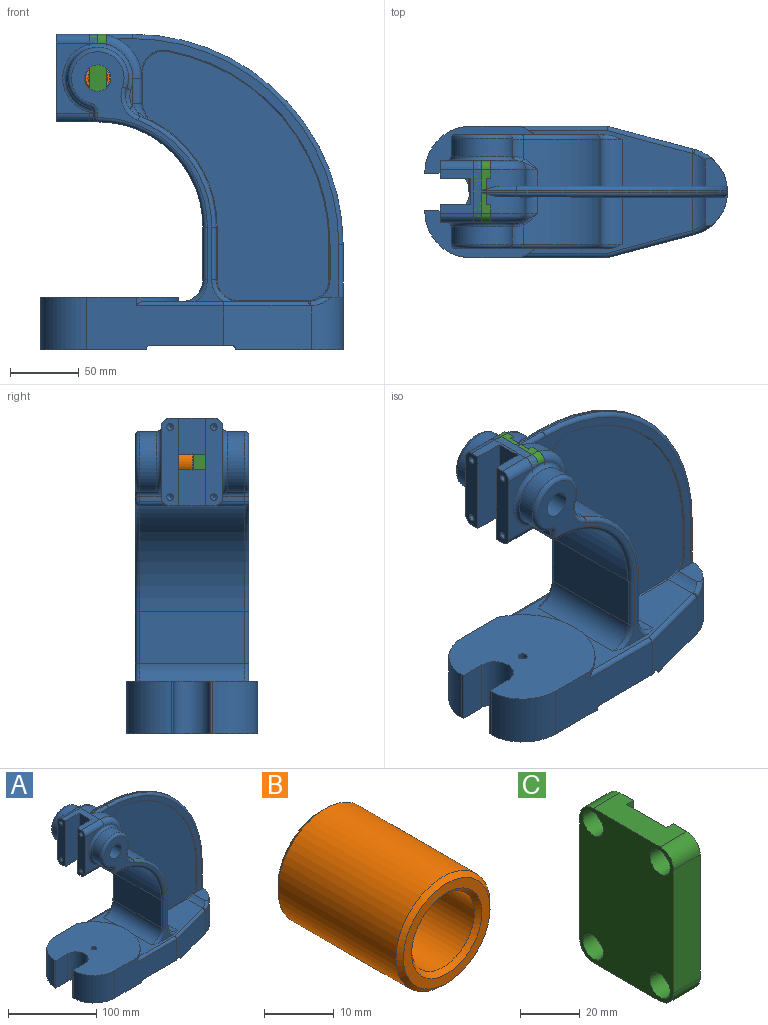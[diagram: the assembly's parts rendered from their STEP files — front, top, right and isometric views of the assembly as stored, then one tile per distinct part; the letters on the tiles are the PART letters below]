
ASSEMBLY  parts=3 mates=2
PART A: 180 faces, bbox 234.5x98.1x244 mm
  f0: plane 63.5x12.7mm, normal (-1,0,0), area 753.5mm2, adj f2,f15,f17,f92,f97,f149,f151,f158
  f1: plane 20.23x2.34mm, normal (0,1,0), area 23.9mm2, adj f90,f91,f104,f106
  f2: plane 50.8x30.1mm, normal (0,-1,0), area 515.4mm2, adj f0,f83,f92,f97,f124
  f3: plane 22.59x12.73mm, normal (1,0,0), area 235.4mm2, adj f19,f26,f32,f87,f94,f174
  f4: plane 22.59x12.73mm, normal (1,0,0), area 235.4mm2, adj f10,f14,f33,f86,f90,f164
  f5: plane 99.19x38.1mm, normal (0,-1,0), area 3202mm2, adj f6,f40,f46,f49,f52,f58,f76,f133
  f6: plane 100x95.25mm, normal (0,0,1), area 7398mm2, adj f5,f43,f44,f48,f54,f55,f56,f57
  f7: plane 38.1x34.96mm, normal (1,0,0), area 1331.9mm2, adj f8,f9,f114,f169
  f8: cylinder r=15.88mm len=34.96mm, axis (0,1,0), area 871.7mm2, adj f7,f37,f115,f167
  f9: cylinder r=85.72mm len=80.21mm, axis (0,1,0), area 3442.3mm2, adj f7,f80,f86,f100,f113,f168
  f10: cylinder r=15.88mm len=18.65mm, axis (0,1,0), area 22.7mm2, adj f4,f11,f33,f162
  f11: cylinder r=142.88mm len=140.67mm, axis (0,1,0), area 163.3mm2, adj f10,f12,f33,f160
  f12: plane 25.4x0.82mm, normal (-1,0,0), area 20.8mm2, adj f11,f13,f33,f161
  f13: cylinder r=15.88mm len=24.81mm, axis (0,1,0), area 242.1mm2, adj f12,f33,f37,f45,f139,f140,f163
  f14: cylinder r=31.75mm len=31.75mm, axis (0,1,0), area 616.8mm2, adj f4,f15,f33,f89,f141
  f15: plane 55.5x31.75mm, normal (0,0,1), area 573.2mm2, adj f0,f14,f16,f19,f31,f88,f92,f141
  f16: plane 63.5x12.7mm, normal (-1,0,0), area 753.5mm2, adj f15,f17,f21,f88,f96,f147,f153,f157
  f17: plane 31.75x30.1mm, normal (0,0,-1), area 533.2mm2, adj f0,f16,f18,f96,f97,f156,f157,f158
  f18: cylinder r=76.2mm len=76.2mm, axis (0,1,0), area 9120.7mm2, adj f17,f22,f103,f105,f119,f121
  f19: cylinder r=31.75mm len=31.75mm, axis (0,1,0), area 616.8mm2, adj f3,f15,f32,f93,f144
  f20: plane 20.23x2.34mm, normal (0,-1,0), area 23.9mm2, adj f94,f95,f122,f124
  f21: plane 50.8x30.1mm, normal (0,1,0), area 515.4mm2, adj f16,f78,f88,f96,f106
  f22: plane 76.2x38.1mm, normal (-1,0,0), area 2903.2mm2, adj f18,f98,f101,f117
  f23: cylinder r=15.88mm len=34.96mm, axis (0,1,0), area 871.7mm2, adj f24,f37,f132,f177
  f24: plane 38.1x34.96mm, normal (1,0,0), area 1331.9mm2, adj f23,f25,f131,f179
  f25: cylinder r=85.72mm len=80.21mm, axis (0,1,0), area 3442.3mm2, adj f24,f81,f87,f118,f130,f178
  f26: cylinder r=15.88mm len=18.65mm, axis (0,1,0), area 22.7mm2, adj f3,f27,f32,f172
  f27: cylinder r=142.88mm len=140.67mm, axis (0,1,0), area 163.3mm2, adj f26,f28,f32,f170
  f28: plane 25.4x0.82mm, normal (-1,0,0), area 20.8mm2, adj f27,f29,f32,f171
  f29: cylinder r=15.88mm len=24.81mm, axis (0,1,0), area 242.1mm2, adj f28,f32,f36,f37,f135,f136,f173
  f30: plane 76.2x7.92mm, normal (1,0,0), area 361.9mm2, adj f31,f36,f42,f45,f51,f53,f143,f146
  f31: cylinder r=152.4mm len=152.4mm, axis (0,1,0), area 377mm2, adj f15,f30,f142,f145
  f32: plane 187.33x160.79mm, normal (0,-1,0), area 1900.4mm2, adj f3,f19,f26,f27,f28,f29,f36,f144
  f33: plane 187.33x160.79mm, normal (0,1,0), area 1900.4mm2, adj f4,f10,f11,f12,f13,f14,f45,f141
  f34: plane 180.67x135mm, normal (0,-1,0), area 14138.8mm2, adj f170,f171,f172,f173,f174,f175,f176,f177
  f35: plane 180.67x135mm, normal (0,1,0), area 14138.8mm2, adj f160,f161,f162,f163,f164,f165,f166,f167
  f36: plane 26.58x18.73mm, normal (0,0,1), area 245.8mm2, adj f29,f30,f32,f53,f136,f146
  f37: plane 119.12x89.67mm, normal (0,0,1), area 4280.2mm2, adj f8,f13,f23,f29,f76,f77,f84,f98
  f38: cylinder r=3.17mm len=9.06mm, axis (0,1,0), area 40.9mm2, adj f40,f42,f52,f69
  f39: cylinder r=3.17mm len=7.93mm, axis (0,1,0), area 39.5mm2, adj f41,f46,f48,f65
  f40: plane 58.73x9.7mm, normal (0,0,-1), area 467.1mm2, adj f5,f38,f49,f52,f64,f69
  f41: plane 58.73x9.7mm, normal (0,0,-1), area 467.1mm2, adj f39,f47,f48,f50,f65,f67
  f42: plane 90.55x77.8mm, normal (0,0,-1), area 1454mm2, adj f30,f38,f47,f50,f51,f52,f53,f59
  f43: plane 38.1x1.61mm, normal (-1,0,0), area 61.5mm2, adj f6,f46,f54,f58
  f44: plane 38.1x1.61mm, normal (-1,0,0), area 61.5mm2, adj f6,f46,f55,f57
  f45: plane 26.58x18.73mm, normal (0,0,1), area 245.8mm2, adj f13,f30,f33,f51,f140,f143
  f46: plane 95.25x76.2mm, normal (0,0,-1), area 2029.8mm2, adj f5,f39,f43,f44,f48,f49,f54,f55
  f47: cylinder r=3.17mm len=9.06mm, axis (0,1,0), area 40.9mm2, adj f41,f42,f50,f67
  f48: plane 99.19x38.1mm, normal (0,1,0), area 3202mm2, adj f6,f39,f41,f46,f50,f57,f76,f137
  f49: cylinder r=3.17mm len=7.93mm, axis (0,1,0), area 39.5mm2, adj f5,f40,f46,f64
  f50: plane 63.64x32.15mm, normal (0.26,0.97,0), area 2053.6mm2, adj f41,f42,f47,f48,f51,f138,f139
  f51: cylinder r=31.75mm len=38.1mm, axis (0,0,-1), area 1379.2mm2, adj f30,f42,f45,f50,f140
  f52: plane 63.64x32.15mm, normal (0.26,-0.97,0), area 2053.6mm2, adj f5,f38,f40,f42,f53,f134,f135
  f53: cylinder r=31.75mm len=38.1mm, axis (0,0,-1), area 1379.2mm2, adj f30,f36,f42,f52,f136
  f54: plane 38.1x19.05mm, normal (0,1,0), area 725.8mm2, adj f6,f43,f46,f56
  f55: plane 38.1x19.05mm, normal (0,-1,0), area 725.8mm2, adj f6,f44,f46,f56
  f56: cylinder r=13.49mm len=38.1mm, axis (0,0,-1), area 1615.1mm2, adj f6,f46,f54,f55
  f57: cylinder r=33.32mm len=38.1mm, axis (0,0,-1), area 1963.7mm2, adj f6,f44,f46,f48
  f58: cylinder r=33.32mm len=38.1mm, axis (0,0,-1), area 1963.7mm2, adj f5,f6,f43,f46
  f59: plane 30.18x6.86mm, normal (-1,0,0), area 207mm2, adj f42,f60,f68,f70
  f60: plane 31.27x5.6mm, normal (0,0,-1), area 124.1mm2, adj f59,f61,f68,f70
  f61: cylinder r=23.8mm len=46.06mm, axis (0,1,0), area 499.2mm2, adj f60,f62,f67,f68,f69,f70
  f62: plane 84.13x79.4mm, normal (0,0,-1), area 5642.5mm2, adj f61,f64,f65,f66,f67,f69
  f63: plane 100.62x79.4mm, normal (0,0,-1), area 6568.5mm2, adj f64,f65,f66,f71,f72,f73,f74,f75
  f64: plane 98.15x30.18mm, normal (0,1,0), area 2718.8mm2, adj f40,f46,f49,f62,f63,f66,f69,f75
  f65: plane 98.15x30.18mm, normal (0,-1,0), area 2718.8mm2, adj f39,f41,f46,f62,f63,f66,f67,f74
  f66: plane 79.4x3.18mm, normal (-1,0,0), area 252.1mm2, adj f62,f63,f64,f65
  f67: plane 62.63x27.36mm, normal (-0.26,-0.97,0), area 1710.8mm2, adj f41,f42,f47,f61,f62,f65,f68
  f68: cylinder r=23.83mm len=30.18mm, axis (0,0,-1), area 814.8mm2, adj f42,f59,f60,f61,f67
  f69: plane 62.63x27.36mm, normal (-0.26,0.97,0), area 1710.8mm2, adj f38,f40,f42,f61,f62,f64,f70
  f70: cylinder r=23.83mm len=30.18mm, axis (0,0,-1), area 814.8mm2, adj f42,f59,f60,f61,f69
  f71: plane 30.18x10.12mm, normal (0,-1,0), area 305.3mm2, adj f46,f63,f73,f75
  f72: plane 30.18x10.12mm, normal (0,1,0), area 305.3mm2, adj f46,f63,f73,f74
  f73: cylinder r=21.42mm len=42.84mm, axis (0,0,-1), area 2030.4mm2, adj f46,f63,f71,f72
  f74: cylinder r=25.4mm len=30.18mm, axis (0,0,-1), area 986.2mm2, adj f46,f63,f65,f72
  f75: cylinder r=25.4mm len=30.18mm, axis (0,0,-1), area 986.2mm2, adj f46,f63,f64,f71
  f76: cylinder r=52.37mm len=95.25mm, axis (0,0,1), area 401mm2, adj f5,f6,f37,f48,f133,f137
  f77: plane 180.98x110.12mm, normal (0,1,0), area 1717.8mm2, adj f37,f85,f99,f101,f103,f109,f110,f111
  f78: plane 16.73x3.98mm, normal (-1,0,0), area 64.1mm2, adj f21,f96,f105,f106,f108,f109
  f79: cylinder r=22.23mm len=44.45mm, axis (0,1,0), area 1356.2mm2, adj f80,f106,f108,f111
  f80: cylinder r=15.88mm len=20.22mm, axis (0,1,0), area 319.4mm2, adj f9,f79,f102,f104,f112
  f81: cylinder r=15.88mm len=20.22mm, axis (0,1,0), area 319.4mm2, adj f25,f82,f120,f122,f129
  f82: cylinder r=22.23mm len=44.45mm, axis (0,1,0), area 1356.2mm2, adj f81,f124,f126,f128
  f83: plane 16.73x3.98mm, normal (-1,0,0), area 64.1mm2, adj f2,f97,f121,f124,f125,f126
  f84: plane 180.98x110.12mm, normal (0,-1,0), area 1717.8mm2, adj f37,f85,f116,f117,f119,f125,f127,f128
  f85: cylinder r=9.53mm len=82.55mm, axis (0,1,0), area 4727mm2, adj f77,f84,f156,f157,f158,f159
  f86: cylinder r=15.88mm len=14.02mm, axis (0,1,0), area 218.9mm2, adj f4,f9,f91,f166
  f87: cylinder r=15.88mm len=14.02mm, axis (0,1,0), area 218.9mm2, adj f3,f25,f95,f176
  f88: cylinder r=6.35mm len=30.1mm, axis (-1,0,0), area 300.2mm2, adj f15,f16,f21,f89
  f89: torus R=25.4mm, axis (0,-1,0), area 461.3mm2, adj f14,f88,f90,f106
  f90: cylinder r=6.35mm len=18.2mm, axis (0,0,1), area 181.6mm2, adj f1,f4,f89,f91
  f91: torus R=22.23mm, axis (0,-1,0), area 98mm2, adj f1,f86,f90,f100,f102
  f92: cylinder r=6.35mm len=30.1mm, axis (1,0,0), area 300.2mm2, adj f0,f2,f15,f93
  f93: torus R=25.4mm, axis (0,-1,0), area 461.3mm2, adj f19,f92,f94,f124
  f94: cylinder r=6.35mm len=18.2mm, axis (0,0,-1), area 181.6mm2, adj f3,f20,f93,f95
  f95: torus R=22.23mm, axis (0,-1,0), area 98mm2, adj f20,f87,f94,f118,f120
  f96: cylinder r=6.35mm len=30.1mm, axis (1,0,0), area 279.1mm2, adj f16,f17,f21,f78,f105
  f97: cylinder r=6.35mm len=30.1mm, axis (-1,0,0), area 279.1mm2, adj f0,f2,f17,f83,f121
  f98: cylinder r=15.88mm len=76.2mm, axis (0,-1,0), area 1900.2mm2, adj f22,f37,f99,f116
  f99: torus R=19.05mm, axis (0,-1,0), area 107.7mm2, adj f37,f77,f98,f101
  f100: bspline ~12.01x8.85mm, area 17.9mm2, adj f9,f91,f102
  f101: cylinder r=3.17mm len=38.1mm, axis (0,0,-1), area 190mm2, adj f22,f77,f99,f103
  f102: bspline ~10.6x9.56mm, area 36.6mm2, adj f80,f91,f100,f104
  f103: torus R=79.38mm, axis (0,-1,0), area 606mm2, adj f18,f77,f101,f107
  f104: torus R=12.7mm, axis (0,-1,0), area 70.6mm2, adj f1,f80,f102,f106
  f105: cylinder r=3.17mm len=22.23mm, axis (0,1,0), area 97.1mm2, adj f18,f78,f96,f107
  f106: torus R=25.4mm, axis (0,-1,0), area 570mm2, adj f1,f21,f78,f79,f89,f104,f108
  f107: sphere r=3.17mm, area 21.6mm2, adj f103,f105,f109
  f108: cylinder r=3.17mm len=15.82mm, axis (0,1,0), area 59.7mm2, adj f78,f79,f106,f110
  f109: cylinder r=3.17mm len=3.98mm, axis (0,0,-1), area 19.9mm2, adj f77,f78,f107,f110
  f110: torus R=6.35mm, axis (0,-1,0), area 28.5mm2, adj f77,f108,f109,f111
  f111: torus R=19.05mm, axis (0,-1,0), area 504.9mm2, adj f77,f79,f110,f112
  f112: torus R=19.05mm, axis (0,-1,0), area 132.1mm2, adj f77,f80,f111,f113
  f113: torus R=82.55mm, axis (0,-1,0), area 510.4mm2, adj f9,f77,f112,f114
  f114: cylinder r=3.17mm len=38.1mm, axis (0,0,1), area 190mm2, adj f7,f77,f113,f115
  f115: torus R=19.05mm, axis (0,-1,0), area 107.7mm2, adj f8,f37,f77,f114
  f116: torus R=19.05mm, axis (0,-1,0), area 107.7mm2, adj f37,f84,f98,f117
  f117: cylinder r=3.17mm len=38.1mm, axis (0,0,1), area 190mm2, adj f22,f84,f116,f119
  f118: bspline ~11.06x8.44mm, area 17.9mm2, adj f25,f95,f120
  f119: torus R=79.38mm, axis (0,-1,0), area 606mm2, adj f18,f84,f117,f123
  f120: bspline ~9.12x8.99mm, area 36.6mm2, adj f81,f95,f118,f122
  f121: cylinder r=3.17mm len=22.23mm, axis (0,1,0), area 97.1mm2, adj f18,f83,f97,f123
  f122: torus R=12.7mm, axis (0,-1,0), area 70.6mm2, adj f20,f81,f120,f124
  f123: sphere r=3.17mm, area 15.8mm2, adj f119,f121,f125
  f124: torus R=25.4mm, axis (0,-1,0), area 570mm2, adj f2,f20,f82,f83,f93,f122,f126
  f125: cylinder r=3.17mm len=3.98mm, axis (0,0,1), area 19.9mm2, adj f83,f84,f123,f127
  f126: cylinder r=3.17mm len=15.82mm, axis (0,1,0), area 59.7mm2, adj f82,f83,f124,f127
  f127: torus R=6.35mm, axis (0,-1,0), area 28.5mm2, adj f84,f125,f126,f128
  f128: torus R=19.05mm, axis (0,-1,0), area 504.9mm2, adj f82,f84,f127,f129
  f129: torus R=19.05mm, axis (0,-1,0), area 132.1mm2, adj f81,f84,f128,f130
  f130: torus R=82.55mm, axis (0,-1,0), area 510.4mm2, adj f25,f84,f129,f131
  f131: cylinder r=3.17mm len=38.1mm, axis (0,0,-1), area 190mm2, adj f24,f84,f130,f132
  f132: torus R=19.05mm, axis (0,-1,0), area 107.7mm2, adj f23,f37,f84,f131
  f133: cylinder r=3.17mm len=63.09mm, axis (1,0,0), area 298.9mm2, adj f5,f37,f76,f134
  f134: cylinder r=3.17mm len=62.81mm, axis (0.97,0.26,0), area 319mm2, adj f37,f52,f133,f135
  f135: bspline ~3.41x3.21mm, area 6mm2, adj f29,f52,f134,f136
  f136: bspline ~18.95x11.92mm, area 79.7mm2, adj f29,f36,f53,f135
  f137: cylinder r=3.17mm len=63.09mm, axis (-1,0,0), area 298.9mm2, adj f37,f48,f76,f138
  f138: cylinder r=3.17mm len=62.81mm, axis (-0.97,0.26,0), area 319mm2, adj f37,f50,f137,f139
  f139: bspline ~6.89x4.84mm, area 6mm2, adj f13,f50,f138,f140
  f140: bspline ~17.46x11.57mm, area 79.7mm2, adj f13,f45,f51,f139
  f141: cylinder r=3.17mm len=25.4mm, axis (-1,0,0), area 92.2mm2, adj f14,f15,f33,f142
  f142: torus R=149.22mm, axis (0,-1,0), area 1184.9mm2, adj f31,f33,f141,f143
  f143: cylinder r=3.17mm len=38.1mm, axis (0,0,1), area 190mm2, adj f30,f33,f45,f142
  f144: cylinder r=3.17mm len=25.4mm, axis (1,0,0), area 92.2mm2, adj f15,f19,f32,f145
  f145: torus R=149.22mm, axis (0,-1,0), area 1184.9mm2, adj f31,f32,f144,f146
  f146: cylinder r=3.17mm len=38.1mm, axis (0,0,-1), area 190mm2, adj f30,f32,f36,f145
  f147: cylinder r=2.38mm len=6.35mm, axis (-1,0,0), area 95mm2, adj f16,f148
  f148: cone r=0mm half-angle=59deg, axis (-1,0,0), area 20.8mm2, adj f147
  f149: cylinder r=2.38mm len=6.35mm, axis (-1,0,0), area 95mm2, adj f0,f150
  f150: cone r=0mm half-angle=59deg, axis (-1,0,0), area 20.8mm2, adj f149
  f151: cylinder r=2.38mm len=6.35mm, axis (-1,0,0), area 95mm2, adj f0,f152
  f152: cone r=0mm half-angle=59deg, axis (-1,0,0), area 20.8mm2, adj f151
  f153: cylinder r=2.38mm len=6.35mm, axis (-1,0,0), area 95mm2, adj f16,f154
  f154: cone r=0mm half-angle=59deg, axis (-1,0,0), area 20.8mm2, adj f153
  f155: cylinder r=3.17mm len=7.93mm, axis (0,0,1), area 158.1mm2, adj f6,f63
  f156: plane 26.47x19.05mm, normal (-1,0,0), area 504.2mm2, adj f17,f85,f157,f158
  f157: plane 63.5x22.17mm, normal (0,-1,0), area 1396.6mm2, adj f15,f16,f17,f85,f156,f159
  f158: plane 63.5x22.17mm, normal (0,1,0), area 1396.6mm2, adj f0,f15,f17,f85,f156,f159
  f159: plane 26.47x19.05mm, normal (-1,0,0), area 504.2mm2, adj f15,f85,f157,f158
  f160: torus R=142.11mm, axis (0,-1,0), area 238.1mm2, adj f11,f35,f161,f162
  f161: cylinder r=0.76mm len=25.4mm, axis (0,0,1), area 30.4mm2, adj f12,f35,f160,f163
  f162: torus R=15.11mm, axis (0,-1,0), area 32.6mm2, adj f10,f35,f160,f164
  f163: torus R=15.11mm, axis (0,-1,0), area 29.3mm2, adj f13,f35,f161,f165
  f164: cylinder r=0.76mm len=22.59mm, axis (0,0,1), area 27mm2, adj f4,f35,f162,f166
  f165: cylinder r=0.76mm len=50.8mm, axis (1,0,0), area 60.8mm2, adj f35,f37,f163,f167
  f166: torus R=15.11mm, axis (0,-1,0), area 20.2mm2, adj f35,f86,f164,f168
  f167: torus R=15.11mm, axis (0,-1,0), area 29.3mm2, adj f8,f35,f165,f169
  f168: torus R=86.49mm, axis (0,-1,0), area 111.5mm2, adj f9,f35,f166,f169
  f169: cylinder r=0.76mm len=38.1mm, axis (0,0,-1), area 45.6mm2, adj f7,f35,f167,f168
  f170: torus R=142.11mm, axis (0,-1,0), area 238.1mm2, adj f27,f34,f171,f172
  f171: cylinder r=0.76mm len=25.4mm, axis (0,0,-1), area 30.4mm2, adj f28,f34,f170,f173
  f172: torus R=15.11mm, axis (0,-1,0), area 32.6mm2, adj f26,f34,f170,f174
  f173: torus R=15.11mm, axis (0,-1,0), area 29.3mm2, adj f29,f34,f171,f175
  f174: cylinder r=0.76mm len=22.59mm, axis (0,0,-1), area 27mm2, adj f3,f34,f172,f176
  f175: cylinder r=0.76mm len=50.8mm, axis (-1,0,0), area 60.8mm2, adj f34,f37,f173,f177
  f176: torus R=15.11mm, axis (0,-1,0), area 20.2mm2, adj f34,f87,f174,f178
  f177: torus R=15.11mm, axis (0,-1,0), area 29.3mm2, adj f23,f34,f175,f179
  f178: torus R=86.49mm, axis (0,-1,0), area 111.5mm2, adj f25,f34,f176,f179
  f179: cylinder r=0.76mm len=38.1mm, axis (0,0,1), area 45.6mm2, adj f24,f34,f177,f178
PART B: 8 faces, bbox 19.1x25.4x19.1 mm
  f0: plane 17.53x17.53mm, normal (0,-1,0), area 82.3mm2, adj f4,f5
  f1: plane 17.53x17.53mm, normal (0,1,0), area 82.3mm2, adj f6,f7
  f2: cylinder r=9.53mm len=23.88mm, axis (0,1,0), area 1428.9mm2, adj f4,f7
  f3: cylinder r=6.35mm len=23.88mm, axis (0,1,0), area 952.6mm2, adj f5,f6
  f4: cone r=9.53mm half-angle=45deg, axis (0,1,0), area 61.9mm2, adj f0,f2
  f5: cone r=6.35mm half-angle=45deg, axis (0,-1,0), area 45.6mm2, adj f0,f3
  f6: cone r=6.35mm half-angle=45deg, axis (0,1,0), area 45.6mm2, adj f1,f3
  f7: cone r=9.53mm half-angle=45deg, axis (0,-1,0), area 61.9mm2, adj f1,f2
PART C: 26 faces, bbox 12.7x44.5x63.5 mm
  f0: plane 63.5x12.7mm, normal (1,0,0), area 753.5mm2, adj f1,f2,f6,f7,f8,f14,f17,f25
  f1: cylinder r=6.35mm len=12.7mm, axis (1,0,0), area 126.7mm2, adj f0,f2,f8,f9
  f2: plane 31.75x12.7mm, normal (0,0,1), area 341.8mm2, adj f0,f1,f3,f9,f10,f23,f24,f25
  f3: cylinder r=6.35mm len=12.7mm, axis (1,0,0), area 126.7mm2, adj f2,f4,f9,f10
  f4: plane 50.8x12.7mm, normal (0,1,0), area 645.2mm2, adj f3,f5,f9,f10
  f5: cylinder r=6.35mm len=12.7mm, axis (1,0,0), area 126.7mm2, adj f4,f6,f9,f10
  f6: plane 31.75x12.7mm, normal (0,0,-1), area 341.8mm2, adj f0,f5,f7,f9,f10,f23,f24,f25
  f7: cylinder r=6.35mm len=12.7mm, axis (1,0,0), area 126.7mm2, adj f0,f6,f8,f9
  f8: plane 50.8x12.7mm, normal (0,-1,0), area 645.2mm2, adj f0,f1,f7,f9
  f9: plane 63.5x44.45mm, normal (-1,0,0), area 2502.9mm2, adj f1,f2,f3,f4,f5,f6,f7,f8
  f10: plane 63.5x12.7mm, normal (1,0,0), area 753.5mm2, adj f2,f3,f4,f5,f6,f11,f20,f24
  f11: cylinder r=2.38mm len=6.35mm, axis (-1,0,0), area 95mm2, adj f10,f12
  f12: plane 9.53x9.53mm, normal (-1,0,0), area 53.4mm2, adj f11,f13
  f13: cylinder r=4.76mm len=9.53mm, axis (-1,0,0), area 190mm2, adj f9,f12
  f14: cylinder r=2.38mm len=6.35mm, axis (-1,0,0), area 95mm2, adj f0,f15
  f15: plane 9.53x9.53mm, normal (-1,0,0), area 53.4mm2, adj f14,f16
  f16: cylinder r=4.76mm len=9.53mm, axis (-1,0,0), area 190mm2, adj f9,f15
  f17: cylinder r=2.38mm len=6.35mm, axis (-1,0,0), area 95mm2, adj f0,f18
  f18: plane 9.53x9.53mm, normal (-1,0,0), area 53.4mm2, adj f17,f19
  f19: cylinder r=4.76mm len=9.53mm, axis (-1,0,0), area 190mm2, adj f9,f18
  f20: cylinder r=2.38mm len=6.35mm, axis (-1,0,0), area 95mm2, adj f10,f21
  f21: plane 9.53x9.53mm, normal (-1,0,0), area 53.4mm2, adj f20,f22
  f22: cylinder r=4.76mm len=9.53mm, axis (-1,0,0), area 190mm2, adj f9,f21
  f23: plane 63.5x19.05mm, normal (1,0,0), area 1209.7mm2, adj f2,f6,f24,f25
  f24: plane 63.5x3.23mm, normal (0,-1,0), area 204.8mm2, adj f2,f6,f10,f23
  f25: plane 63.5x3.23mm, normal (0,1,0), area 204.8mm2, adj f0,f2,f6,f23
PLACE A t=(-47.39,-19.81,34.76)mm
PLACE B t=(-47.39,-36.44,34.76)mm
PLACE C t=(-10.94,-19.81,34.76)mm
MATE fastened B.f2 <-> A.f14  axis (0,1,0) through (-47.39,-19.81,34.76)mm
MATE fastened C.f14 <-> A.f149  axis (-1,0,0) through (-47.39,-35.68,60.16)mm
